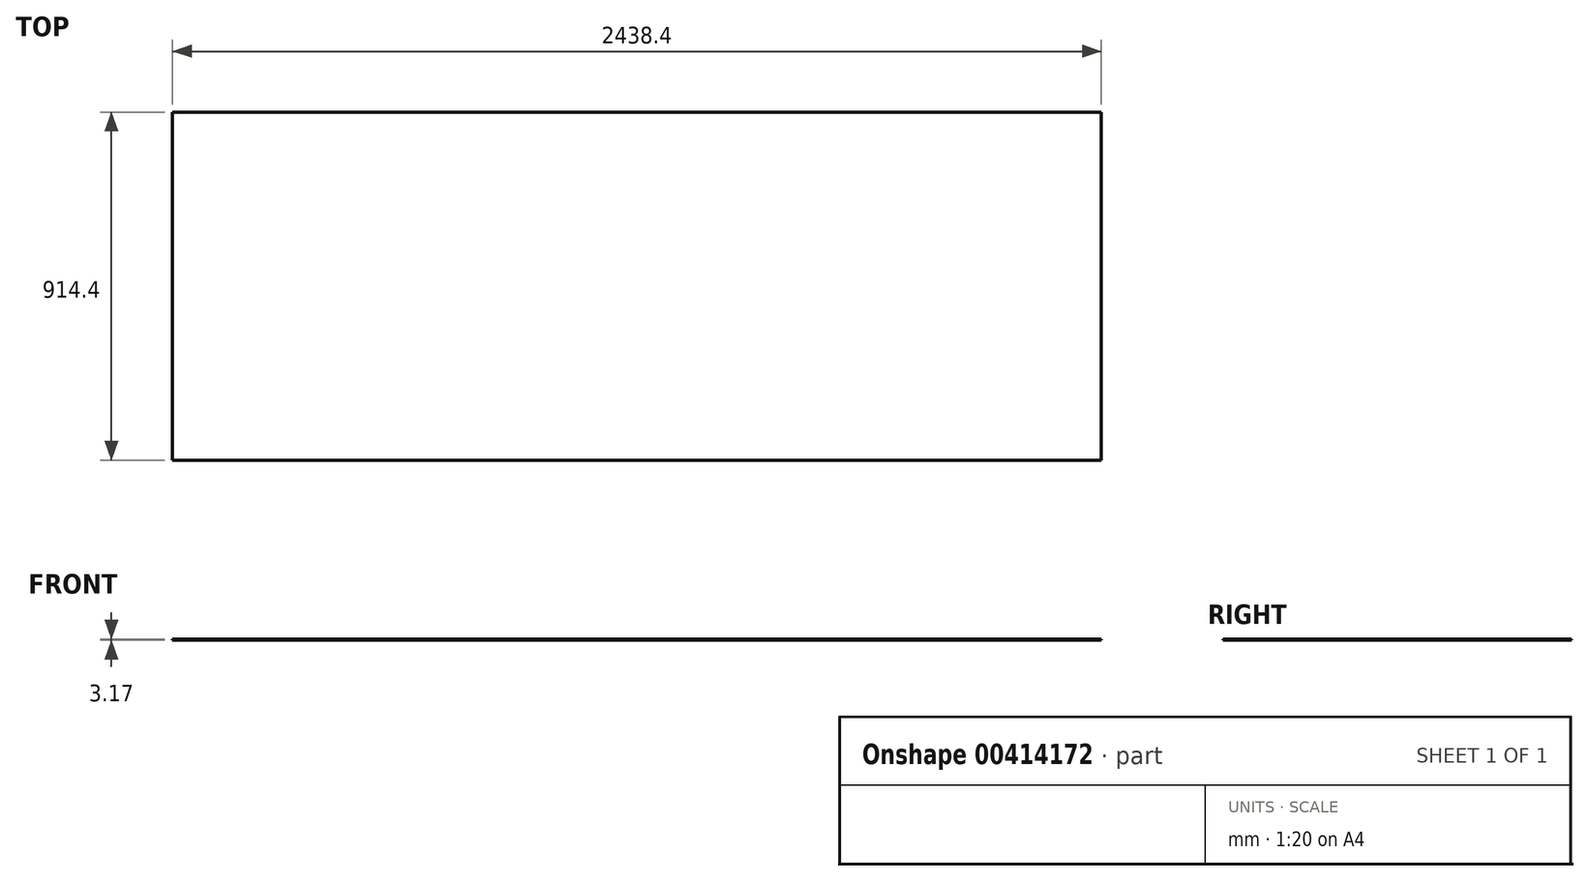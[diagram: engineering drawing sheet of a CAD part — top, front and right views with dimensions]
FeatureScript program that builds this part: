
annotation { "Feature Type Name" : "Feature", "Feature Type Description" : "" }
export const myFeature = defineFeature(function(context is Context, id is Id, definition is map)
    precondition{}
    {
        {
            var Q0;
            Q0=qCreatedBy(makeId("Top.planeOp"),FACE);
            var sketch = newSketch(context, id + "F0", { "sketchPlane" : qUnion([Q0])});
            skLineSegment(sketch, "E0.bottom", {"start": v(-1219.2, 457.2) * mm, "end": v(1219.2, 457.2) * mm});
            skLineSegment(sketch, "E0.top", {"start": v(-1219.2, -457.2) * mm, "end": v(1219.2, -457.2) * mm});
            skLineSegment(sketch, "E0.left", {"start": v(-1219.2, 457.2) * mm, "end": v(-1219.2, -457.2) * mm});
            skLineSegment(sketch, "E0.right", {"start": v(1219.2, 457.2) * mm, "end": v(1219.2, -457.2) * mm});
            skSolve(sketch);
        }
        {
            var Q0;
            Q0 = qSketchRegion(id + "F0", true);
            extrude(context, id + "F1", {"entities" : qUnion([Q0]), "depth" : 3.17 * mm});
        }
    });
